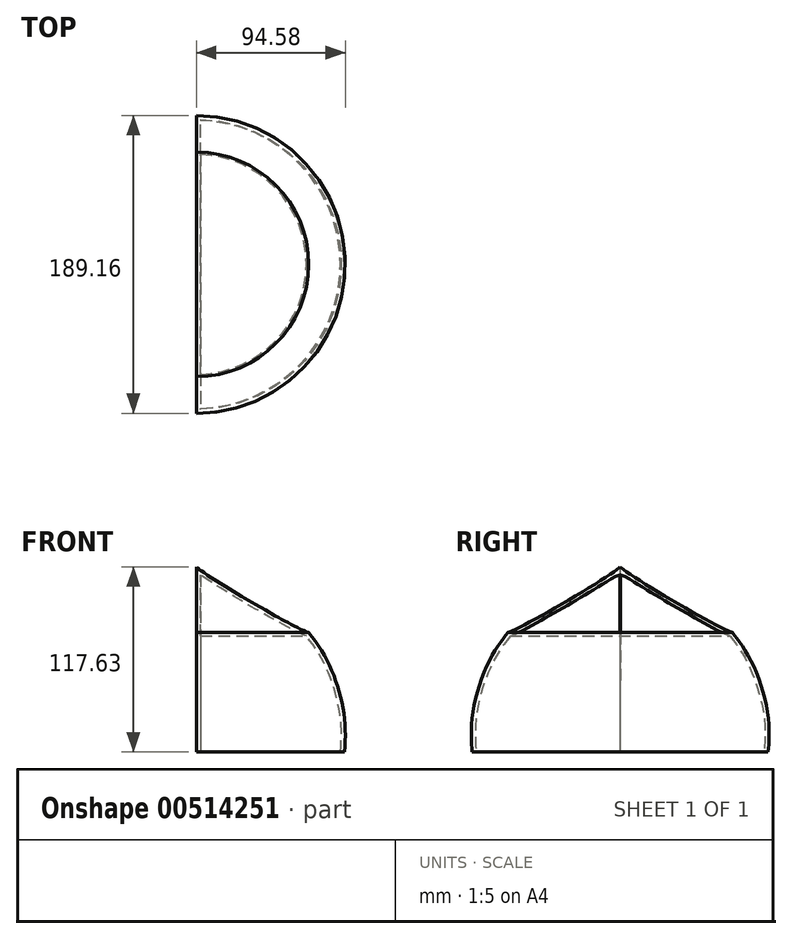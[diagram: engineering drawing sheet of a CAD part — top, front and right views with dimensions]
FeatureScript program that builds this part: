
annotation { "Feature Type Name" : "Feature", "Feature Type Description" : "" }
export const myFeature = defineFeature(function(context is Context, id is Id, definition is map)
    precondition{}
    {
        {
            var Q0;
            Q0=qCreatedBy(makeId("Top.planeOp"),FACE);
            var sketch = newSketch(context, id + "F0", { "sketchPlane" : qUnion([Q0])});
            skFitSpline(sketch, "E0.0", {"points": [v(-10.02, 93.7) * mm, v(-9.88, 93.71) * mm, v(-9.75, 93.72) * mm, v(-9.6, 93.73) * mm, v(-7.33, 93.86) * mm, v(-5.05, 93.95) * mm, v(-2.78, 94) * mm, v(-2.2, 94) * mm, v(-1.6, 94) * mm, v(-1.02, 94.01) * mm, v(-0.43, 94.01) * mm, v(0.16, 94.01) * mm, v(0.75, 94.01) * mm, v(1.94, 94) * mm, v(3.13, 93.99) * mm, v(4.31, 93.96) * mm, v(6.7, 93.9) * mm, v(9.06, 93.78) * mm, v(11.43, 93.6) * mm, v(16.17, 93.27) * mm, v(20.9, 92.73) * mm, v(25.6, 91.97) * mm, v(27.91, 91.6) * mm, v(31.39, 90.96) * mm, v(36, 89.95) * mm, v(38.3, 89.38) * mm, v(39.45, 89.1) * mm, v(43.98, 87.93) * mm, v(48.43, 86.57) * mm, v(52.78, 85) * mm, v(57.07, 83.46) * mm, v(61.26, 81.73) * mm, v(65.37, 79.78) * mm, v(66.77, 79.12) * mm, v(68.86, 78.09) * mm, v(71.6, 76.64) * mm, v(73.65, 75.5) * mm, v(75.68, 74.34) * mm, v(77.7, 73.13) * mm, v(79.7, 71.91) * mm, v(81.04, 71.1) * mm, v(81.7, 70.7) * mm]});
            skFitSpline(sketch, "E0.1", {"points": [v(73.77, 59.33) * mm, v(73.77, 64.7) * mm, v(73.77, 70.07) * mm, v(73.77, 75.43) * mm]});
            skLineSegment(sketch, "E0.2", {"start": v(73.77, 59.33) * mm, "end": v(93.41, -0.46) * mm});
            skLineSegment(sketch, "E0.3", {"start": v(73.77, -59.33) * mm, "end": v(93.41, -0.46) * mm});
            skFitSpline(sketch, "E0.4", {"points": [v(73.77, -59.33) * mm, v(73.77, -64.7) * mm, v(73.77, -70.07) * mm, v(73.77, -75.43) * mm]});
            skFitSpline(sketch, "E0.5", {"points": [v(175.74, -13.82) * mm, v(171.1, -16.63) * mm, v(161.8, -22.24) * mm, v(147.88, -30.67) * mm, v(133.96, -39.1) * mm, v(122.35, -46.11) * mm, v(113.07, -51.73) * mm, v(106.1, -55.94) * mm, v(99.14, -60.15) * mm, v(93.34, -63.66) * mm, v(88.7, -66.47) * mm, v(85.21, -68.58) * mm, v(81.73, -70.68) * mm, v(78.83, -72.44) * mm, v(76.5, -73.85) * mm, v(74.76, -74.88) * mm, v(72.99, -75.88) * mm, v(70.6, -77.18) * mm, v(67.6, -78.73) * mm, v(65.14, -79.9) * mm, v(63.9, -80.47) * mm, v(61.63, -81.51) * mm, v(59.32, -82.5) * mm, v(56.97, -83.43) * mm, v(54.61, -84.36) * mm, v(52.22, -85.23) * mm, v(49.8, -86.04) * mm, v(47.36, -86.85) * mm, v(44.9, -87.6) * mm, v(42.4, -88.3) * mm, v(41.13, -88.65) * mm, v(38.6, -89.32) * mm, v(36.04, -89.93) * mm, v(34.77, -90.21) * mm, v(32.16, -90.8) * mm, v(29.55, -91.3) * mm, v(26.93, -91.75) * mm, v(24.25, -92.2) * mm, v(21.57, -92.6) * mm, v(18.88, -92.9) * mm, v(13.35, -93.56) * mm, v(7.79, -93.92) * mm, v(2.2, -94) * mm, v(1.48, -94) * mm, v(0.77, -94.01) * mm, v(0.06, -94.01) * mm, v(-0.66, -94.01) * mm, v(-1.38, -94) * mm, v(-2.1, -94) * mm, v(-3.55, -93.98) * mm, v(-5, -93.94) * mm, v(-6.47, -93.88) * mm, v(-6.99, -93.86) * mm, v(-7.5, -93.84) * mm, v(-8.03, -93.81) * mm]});
            skFitSpline(sketch, "E0.6", {"points": [v(0, 0) * mm, v(0, -23.68) * mm, v(0, -47.35) * mm, v(0, -71.03) * mm]});
            skFitSpline(sketch, "E0.7", {"points": [v(0, -71.03) * mm, v(0, -78.69) * mm, v(0, -86.35) * mm, v(0, -94.01) * mm]});
            skFitSpline(sketch, "E0.8", {"points": [v(0, 0) * mm, v(0, 23.68) * mm, v(0, 47.35) * mm, v(0, 71.03) * mm]});
            skFitSpline(sketch, "E0.9", {"points": [v(0, 71.03) * mm, v(0, 78.69) * mm, v(0, 86.35) * mm, v(0, 94.01) * mm]});
            skLineSegment(sketch, "E1", {"start": v(0, 0) * mm, "end": v(93.41, -0.46) * mm, "construction": true});
            skLineSegment(sketch, "E2", {"start": v(0, 0) * mm, "end": v(73.77, 75.43) * mm, "construction": true});
            skSolve(sketch);
        }
        {
            var Q0;
            Q0=qCreatedBy(makeId("Right.planeOp"),FACE);
            var sketch = newSketch(context, id + "F1", { "sketchPlane" : qUnion([Q0])});
            skFitSpline(sketch, "E3.1", {"points": [v(0, 117.63) * mm, v(6.9, 116.3) * mm, v(20.44, 112.46) * mm, v(39.51, 103.35) * mm, v(56.78, 91.17) * mm, v(66.75, 81.22) * mm, v(71.29, 75.87) * mm, v(0, 117.63) * mm]});
            skFitSpline(sketch, "E3.2", {"points": [v(71.29, 75.87) * mm, v(75.37, 70.5) * mm, v(82.57, 59.03) * mm, v(90.12, 40.17) * mm, v(94.18, 20.27) * mm, v(94.47, 6.73) * mm, v(94.01, 0) * mm]});
            skLineSegment(sketch, "E4", {"start": v(0, 117.63) * mm, "end": v(0, 0) * mm});
            skFitSpline(sketch, "E5", {"points": [v(0, 117.63) * mm, v(6.9, 116.3) * mm, v(20.44, 112.46) * mm, v(39.51, 103.35) * mm, v(56.78, 91.17) * mm, v(66.75, 81.22) * mm, v(71.29, 75.87) * mm]});
            skLineSegment(sketch, "E6", {"start": v(0, 0) * mm, "end": v(94.01, 0) * mm});
            skSolve(sketch);
        }
        {
            var Q0;
            Q0=sQuery(id+"F0.wireOp",EDGE,"E2");
            var Q1;
            Q1=qCreatedBy(makeId("Front.planeOp"),FACE);
            cPlane(context, id + "F2", {"entities" : qUnion([Q0, Q1]), "cplaneType" : CPlaneType.LINE_ANGLE, "offset" : 25 * mm, "angle" : 0 * degree, "width" : 150 * mm, "height" : 150 * mm});
        }
        {
            var Q0;
            Q0=qCreatedBy(makeId("Front.planeOp"),FACE);
            var sketch = newSketch(context, id + "F3", { "sketchPlane" : qUnion([Q0])});
            skFitSpline(sketch, "E7.1", {"points": [v(0, 117.63) * mm, v(6.89, 116.3) * mm, v(20.44, 112.46) * mm, v(39.51, 103.35) * mm, v(56.78, 91.17) * mm, v(66.75, 81.22) * mm, v(71.29, 75.87) * mm]});
            skFitSpline(sketch, "E7.2", {"points": [v(71.18, 76.01) * mm, v(75.23, 70.62) * mm, v(82.35, 59.1) * mm, v(89.78, 40.2) * mm, v(93.71, 20.27) * mm, v(93.92, 6.73) * mm, v(93.41, 0) * mm]});
            skLineSegment(sketch, "E8", {"start": v(0, 117.63) * mm, "end": v(0, 0) * mm});
            skLineSegment(sketch, "E9", {"start": v(-0.6, 0) * mm, "end": v(93.41, 0) * mm});
            skSolve(sketch);
        }
        {
            var Q0;
            Q0=makeQuery(id+"F1.imprint","IMPRINT",FACE,{"disambiguationData":[TD([[makeQuery(id+"F1.imprint","IMPRINT",EDGE,{"derivedFrom":sQuery(id+"F1.wireOp",EDGE,"E3.2")}),-1.0]])]});
            var Q1;
            Q1=sQuery(id+"F3.wireOp",EDGE,"E8");
            revolve(context, id + "F4", {"entities" : qUnion([Q0]), "axis" : qUnion([Q1]), "revolveType" : RevolveType.ONE_DIRECTION, "angle" : 180 * degree});
        }
        {
            var Q0;
            Q0=makeQuery(id+"F4.opRevolve","SWEPT_FACE",FACE,{"disambiguationData":[OSD([sQuery(id+"F1.wireOp",EDGE,"E6")])]});
            shell(context, id + "F5", {"entities" : qUnion([Q0]), "thickness" : 2.5 * mm});
        }
    });
